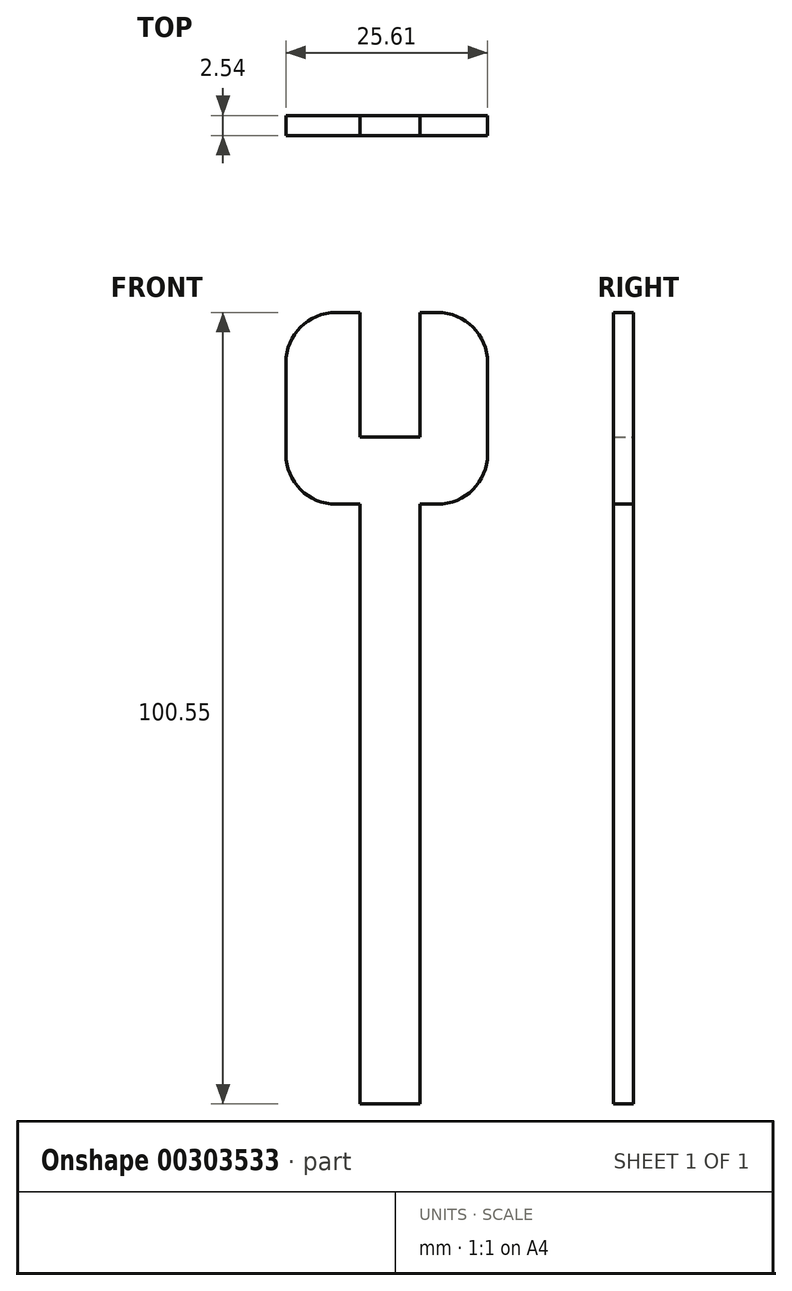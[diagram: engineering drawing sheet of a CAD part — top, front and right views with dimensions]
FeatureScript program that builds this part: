
annotation { "Feature Type Name" : "Feature", "Feature Type Description" : "" }
export const myFeature = defineFeature(function(context is Context, id is Id, definition is map)
    precondition{}
    {
        {
            var Q0;
            Q0=qCreatedBy(makeId("Front.planeOp"),FACE);
            var sketch = newSketch(context, id + "F0", { "sketchPlane" : qUnion([Q0])});
            skLineSegment(sketch, "E0", {"start": v(-32.75, 29.47) * mm, "end": v(-32.75, -46.73) * mm});
            skLineSegment(sketch, "E1", {"start": v(-40.37, 29.47) * mm, "end": v(-40.37, -46.73) * mm});
            skLineSegment(sketch, "E2", {"start": v(-40.37, 29.47) * mm, "end": v(-43.44, 29.47) * mm});
            skLineSegment(sketch, "E3", {"start": v(-49.8, 35.82) * mm, "end": v(-49.8, 47.47) * mm});
            skLineSegment(sketch, "E4", {"start": v(-32.75, 29.47) * mm, "end": v(-30.53, 29.47) * mm});
            skLineSegment(sketch, "E5", {"start": v(-24.18, 35.82) * mm, "end": v(-24.18, 47.47) * mm});
            skLineSegment(sketch, "E6", {"start": v(-43.44, 53.82) * mm, "end": v(-40.37, 53.82) * mm});
            skLineSegment(sketch, "E7", {"start": v(-40.37, 53.82) * mm, "end": v(-40.37, 38) * mm});
            skLineSegment(sketch, "E8", {"start": v(-40.37, 38) * mm, "end": v(-32.75, 38) * mm});
            skLineSegment(sketch, "E9", {"start": v(-32.75, 38) * mm, "end": v(-32.75, 53.82) * mm});
            skLineSegment(sketch, "E10", {"start": v(-32.75, 53.82) * mm, "end": v(-30.53, 53.82) * mm});
            skLineSegment(sketch, "E11", {"start": v(-40.37, -46.73) * mm, "end": v(-32.75, -46.73) * mm});
            skPoint(sketch, "E12.visualSharp", {"position": v(-49.8, 29.47) * mm});
            skArc(sketch, "E12.filletArc", {"start": v(-49.8, 35.82) * mm, "mid": v(-47.93, 31.33) * mm, "end": v(-43.44, 29.47) * mm});
            skPoint(sketch, "E13.visualSharp", {"position": v(-49.8, 53.82) * mm});
            skArc(sketch, "E13.filletArc", {"start": v(-43.44, 53.82) * mm, "mid": v(-47.93, 51.96) * mm, "end": v(-49.8, 47.47) * mm});
            skPoint(sketch, "E14.visualSharp", {"position": v(-24.18, 53.82) * mm});
            skArc(sketch, "E14.filletArc", {"start": v(-24.18, 47.47) * mm, "mid": v(-26.04, 51.96) * mm, "end": v(-30.53, 53.82) * mm});
            skPoint(sketch, "E15.visualSharp", {"position": v(-24.18, 29.47) * mm});
            skArc(sketch, "E15.filletArc", {"start": v(-30.53, 29.47) * mm, "mid": v(-26.04, 31.33) * mm, "end": v(-24.18, 35.82) * mm});
            skSolve(sketch);
        }
        {
            var Q0;
            Q0=makeQuery(id+"F0.imprint","IMPRINT",FACE,{"disambiguationData":[TD([[makeQuery(id+"F0.imprint","IMPRINT",EDGE,{"derivedFrom":sQuery(id+"F0.wireOp",EDGE,"E0")}),-1.0]])]});
            extrude(context, id + "F1", {"entities" : qUnion([Q0]), "depth" : 2.54 * mm});
        }
    });
